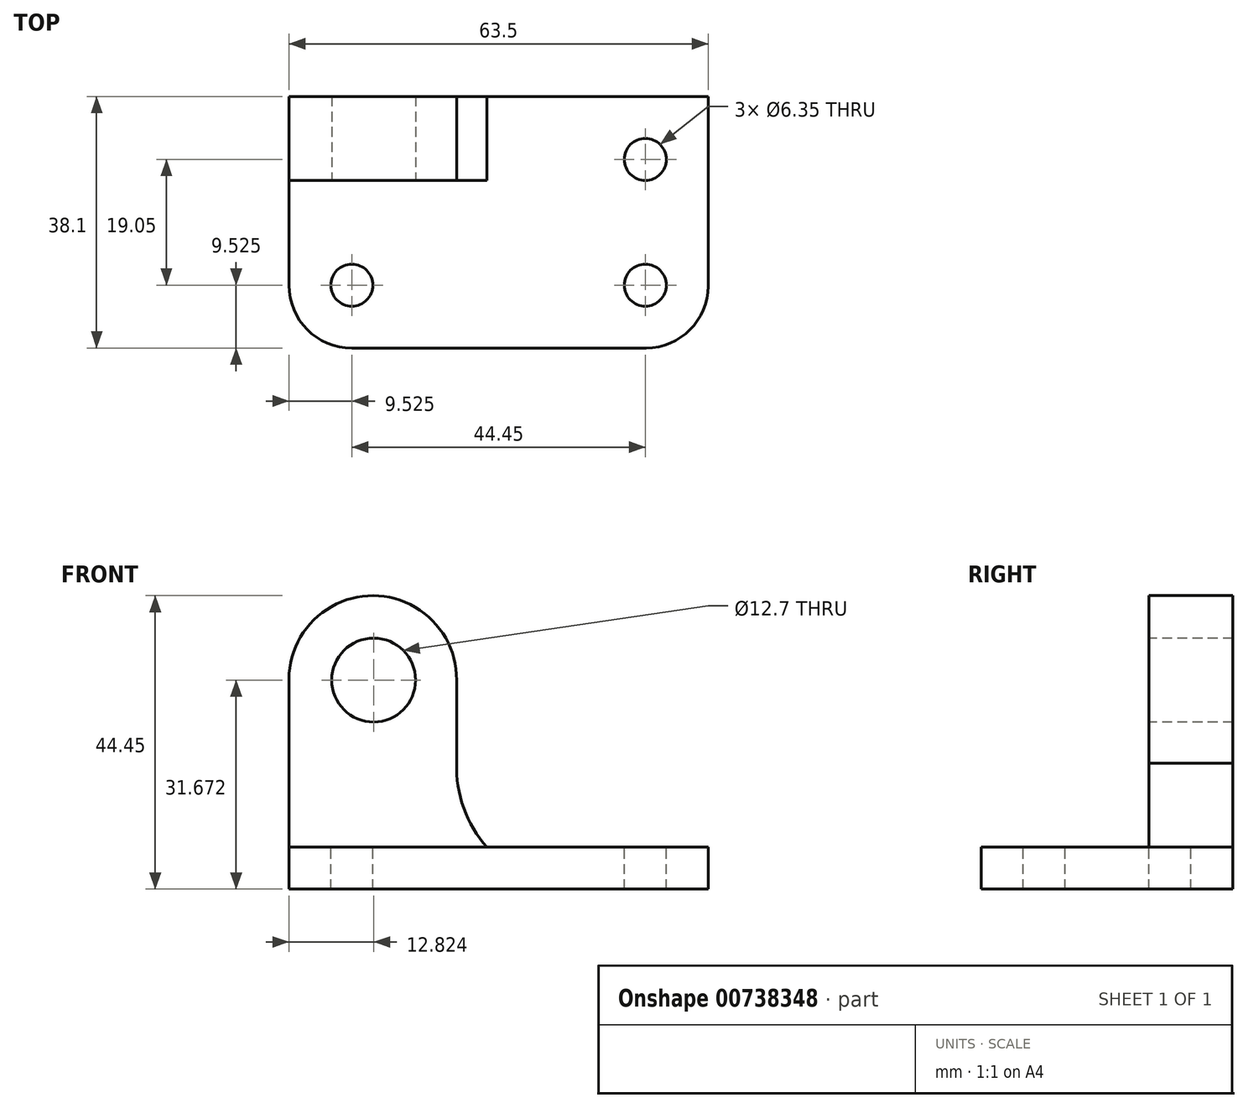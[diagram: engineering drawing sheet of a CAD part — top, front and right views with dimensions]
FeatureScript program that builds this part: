
annotation { "Feature Type Name" : "Feature", "Feature Type Description" : "" }
export const myFeature = defineFeature(function(context is Context, id is Id, definition is map)
    precondition{}
    {
        {
            var Q0;
            Q0=qCreatedBy(makeId("Right.planeOp"),FACE);
            var sketch = newSketch(context, id + "F0", { "sketchPlane" : qUnion([Q0])});
            skLineSegment(sketch, "E0", {"start": v(0, 0) * mm, "end": v(0, 44.45) * mm});
            skLineSegment(sketch, "E1", {"start": v(0, 44.45) * mm, "end": v(-12.7, 44.45) * mm});
            skLineSegment(sketch, "E2", {"start": v(-12.7, 44.45) * mm, "end": v(-12.7, 6.35) * mm});
            skLineSegment(sketch, "E3", {"start": v(-12.7, 6.35) * mm, "end": v(-38.1, 6.35) * mm});
            skLineSegment(sketch, "E4", {"start": v(-38.1, 6.35) * mm, "end": v(-38.1, 0) * mm});
            skLineSegment(sketch, "E5", {"start": v(-38.1, 0) * mm, "end": v(0, 0) * mm});
            skSolve(sketch);
        }
        {
            var Q0;
            Q0 = qSketchRegion(id + "F0", true);
            extrude(context, id + "F1", {"entities" : qUnion([Q0]), "depth" : 63.5 * mm, "offsetDistance" : 25.4 * mm});
        }
        {
            var Q0;
            Q0=makeQuery(id+"F1.opExtrude","SWEPT_FACE",FACE,{"disambiguationData":[OSD([sQuery(id+"F0.wireOp",EDGE,"E2")])]});
            var sketch = newSketch(context, id + "F2", { "sketchPlane" : qUnion([Q0])});
            skCircle(sketch, "E6", {"center": v(12.82, 31.67) * mm, "radius": 6.35 * mm});
            skArc(sketch, "E7", {"start": v(25.4, 19.1) * mm, "mid": v(26.49, 12.25) * mm, "end": v(30.03, 6.3) * mm});
            skLineSegment(sketch, "E8", {"start": v(25.4, 31.67) * mm, "end": v(25.4, 19.1) * mm});
            skLineSegment(sketch, "E9", {"start": v(0, 31.67) * mm, "end": v(0, 6.34) * mm});
            skLineSegment(sketch, "E10", {"start": v(0, 6.34) * mm, "end": v(30.03, 6.3) * mm});
            skLineSegment(sketch, "E11", {"start": v(0, 31.67) * mm, "end": v(25.4, 31.67) * mm});
            skLineSegment(sketch, "E12", {"start": v(0, 31.67) * mm, "end": v(0, 44.45) * mm});
            skArc(sketch, "E13", {"start": v(25.4, 31.67) * mm, "mid": v(12.7, 44.45) * mm, "end": v(0, 31.67) * mm});
            skSolve(sketch);
        }
        {
            var Q0;
            {var subQ0=sQuery(id+"F2.wireOp",EDGE,"E11");var subQ1=sQuery(id+"F2.wireOp",EDGE,"E6");var subQ2=makeQuery(id+"F2.imprint","INTERSECT",VERTEX,{"disambiguationData":[OD(0.0)],"derivedFrom":[subQ1,subQ0]});Q0=makeQuery(id+"F2.imprint","IMPRINT",FACE,{"disambiguationData":[TD([[makeQuery(id+"F2.imprint","IMPRINT",EDGE,{"disambiguationData":[TD([[subQ2,1.0]])],"derivedFrom":subQ1}),1.0]])]});}
            var Q1;
            {var subQ0=sQuery(id+"F2.wireOp",EDGE,"E11");var subQ1=sQuery(id+"F2.wireOp",EDGE,"E6");var subQ2=makeQuery(id+"F2.imprint","INTERSECT",VERTEX,{"disambiguationData":[OD(0.0)],"derivedFrom":[subQ1,subQ0]});Q1=makeQuery(id+"F2.imprint","IMPRINT",FACE,{"disambiguationData":[TD([[makeQuery(id+"F2.imprint","IMPRINT",EDGE,{"disambiguationData":[TD([[subQ2,-1.0]])],"derivedFrom":subQ1}),1.0]])]});}
            var Q2;
            {var subQ5=sQuery(id+"F2.wireOp",EDGE,"E8");Q2=makeQuery(id+"F2.imprint","IMPRINT",FACE,{"disambiguationData":[TD([[makeQuery(id+"F2.imprint","IMPRINT",EDGE,{"derivedFrom":subQ5}),1.0]])]});}
            extrude(context, id + "F3", {"entities" : qUnion([Q0, Q1, Q2]), "operationType" : NewBodyOperationType.REMOVE, "endBound" : BoundingType.THROUGH_ALL, "oppositeDirection" : true, "depth" : 25.4 * mm, "offsetDistance" : 25.4 * mm});
        }
        {
            var Q0;
            {var subQ0=sQuery(id+"F0.wireOp",EDGE,"E3");Q0=makeQuery(id+"F3.boolean.opBoolean","MERGE",FACE,{"derivedFrom":[makeQuery(id+"F1.opExtrude","SWEPT_FACE",FACE,{"disambiguationData":[OSD([subQ0])]}),makeQuery(id+"F3.opExtrude","SWEPT_FACE",FACE,{"disambiguationData":[OSD([sQuery(id+"F0.wireOp",EDGE,"E2"),subQ0])]})]});}
            var sketch = newSketch(context, id + "F4", { "sketchPlane" : qUnion([Q0])});
            skLineSegment(sketch, "E14", {"start": v(0, -38.1) * mm, "end": v(0, -28.58) * mm});
            skLineSegment(sketch, "E15", {"start": v(0, -28.58) * mm, "end": v(9.53, -28.58) * mm});
            skCircle(sketch, "E16", {"center": v(9.53, -28.58) * mm, "radius": 3.18 * mm});
            skArc(sketch, "E17", {"start": v(0, -28.58) * mm, "mid": v(2.79, -35.31) * mm, "end": v(9.52, -38.1) * mm});
            skLineSegment(sketch, "E18", {"start": v(63.5, -28.58) * mm, "end": v(53.98, -28.58) * mm});
            skLineSegment(sketch, "E19", {"start": v(53.98, -28.57) * mm, "end": v(53.98, -38.1) * mm});
            skCircle(sketch, "E20", {"center": v(53.98, -28.58) * mm, "radius": 3.18 * mm});
            skArc(sketch, "E21", {"start": v(53.98, -38.1) * mm, "mid": v(60.73, -35.33) * mm, "end": v(63.5, -28.58) * mm});
            skSolve(sketch);
        }
        {
            var Q0;
            Q0=makeQuery(id+"F4.imprint","IMPRINT",FACE,{"disambiguationData":[TD([[makeQuery(id+"F4.imprint","IMPRINT",EDGE,{"derivedFrom":sQuery(id+"F4.wireOp",EDGE,"E16")}),1.0]])]});
            var Q1;
            {var subQ0=sQuery(id+"F4.wireOp",EDGE,"E19");var subQ1=sQuery(id+"F4.wireOp",EDGE,"E18");var subQ2=makeQuery(id+"F4.imprint","INTERSECT",VERTEX,{"derivedFrom":[subQ1,subQ0]});Q1=makeQuery(id+"F4.imprint","IMPRINT",FACE,{"disambiguationData":[TD([[makeQuery(id+"F4.imprint","IMPRINT",EDGE,{"disambiguationData":[TD([[subQ2,1.0]])],"derivedFrom":subQ1}),-1.0]])]});}
            var Q2;
            {var subQ0=sQuery(id+"F4.wireOp",EDGE,"E19");var subQ1=sQuery(id+"F4.wireOp",EDGE,"E18");var subQ2=makeQuery(id+"F4.imprint","INTERSECT",VERTEX,{"derivedFrom":[subQ1,subQ0]});Q2=makeQuery(id+"F4.imprint","IMPRINT",FACE,{"disambiguationData":[TD([[makeQuery(id+"F4.imprint","IMPRINT",EDGE,{"disambiguationData":[TD([[subQ2,1.0]])],"derivedFrom":subQ1}),1.0]])]});}
            var Q3;
            {var subQ0=sQuery(id+"F4.wireOp",EDGE,"E21");var subQ1=makeQuery(id+"F1.opExtrude","SWEPT_EDGE",EDGE,{"disambiguationData":[OSD([sQuery(id+"F0.wireOp",EDGE,"E3"),sQuery(id+"F0.wireOp",EDGE,"E4")])]});var subQ3=makeQuery(id+"F4.imprint","INTERSECT",VERTEX,{"derivedFrom":[subQ1,subQ0]});Q3=makeQuery(id+"F4.imprint","IMPRINT",FACE,{"disambiguationData":[TD([[makeQuery(id+"F4.imprint","IMPRINT",EDGE,{"disambiguationData":[TD([[subQ3,1.0]])],"derivedFrom":subQ0}),1.0]])]});}
            var Q4;
            {var subQ0=sQuery(id+"F4.wireOp",EDGE,"E21");var subQ1=sQuery(id+"F0.wireOp",EDGE,"E3");var subQ2=makeQuery(id+"F3.boolean.opBoolean","MERGE",EDGE,{"derivedFrom":[makeQuery(id+"F1.opExtrude","CAP_EDGE",EDGE,{"disambiguationData":[OSD([subQ1])],"isStart":false}),makeQuery(id+"F3.opExtrude","SWEPT_EDGE",EDGE,{"disambiguationData":[OSD([sQuery(id+"F0.wireOp",EDGE,"E2"),subQ1])]})]});var subQ4=makeQuery(id+"F4.imprint","INTERSECT",VERTEX,{"derivedFrom":[subQ2,subQ0]});Q4=makeQuery(id+"F4.imprint","IMPRINT",FACE,{"disambiguationData":[TD([[makeQuery(id+"F4.imprint","IMPRINT",EDGE,{"disambiguationData":[TD([[subQ4,-1.0]])],"derivedFrom":subQ0}),1.0]])]});}
            var Q5;
            {var subQ0=sQuery(id+"F4.wireOp",EDGE,"E14");Q5=makeQuery(id+"F4.imprint","IMPRINT",FACE,{"disambiguationData":[TD([[makeQuery(id+"F4.imprint","IMPRINT",EDGE,{"derivedFrom":subQ0}),1.0]])]});}
            var Q6;
            {var subQ0=sQuery(id+"F4.wireOp",EDGE,"E21");var subQ1=sQuery(id+"F0.wireOp",EDGE,"E3");var subQ2=makeQuery(id+"F1.opExtrude","SWEPT_EDGE",EDGE,{"disambiguationData":[OSD([subQ1,sQuery(id+"F0.wireOp",EDGE,"E4")])]});var subQ3=makeQuery(id+"F4.imprint","INTERSECT",VERTEX,{"derivedFrom":[subQ2,subQ0]});Q6=makeQuery(id+"F4.imprint","IMPRINT",FACE,{"disambiguationData":[TD([[makeQuery(id+"F4.imprint","IMPRINT",EDGE,{"disambiguationData":[TD([[subQ3,-1.0]])],"derivedFrom":subQ0}),-1.0]])]});}
            extrude(context, id + "F5", {"entities" : qUnion([Q0, Q1, Q2, Q3, Q4, Q5, Q6]), "operationType" : NewBodyOperationType.REMOVE, "endBound" : BoundingType.THROUGH_ALL, "oppositeDirection" : true, "depth" : 25.4 * mm, "offsetDistance" : 25.4 * mm});
        }
        {
            var Q0;
            {var subQ0=sQuery(id+"F0.wireOp",EDGE,"E3");Q0=makeQuery(id+"F3.boolean.opBoolean","MERGE",FACE,{"derivedFrom":[makeQuery(id+"F1.opExtrude","SWEPT_FACE",FACE,{"disambiguationData":[OSD([subQ0])]}),makeQuery(id+"F3.opExtrude","SWEPT_FACE",FACE,{"disambiguationData":[OSD([sQuery(id+"F0.wireOp",EDGE,"E2"),subQ0])]})]});}
            var sketch = newSketch(context, id + "F6", { "sketchPlane" : qUnion([Q0])});
            skLineSegment(sketch, "E22", {"start": v(53.98, -28.57) * mm, "end": v(53.98, 0) * mm});
            skLineSegment(sketch, "E23", {"start": v(53.98, 0) * mm, "end": v(53.98, -9.53) * mm});
            skCircle(sketch, "E24", {"center": v(53.98, -9.53) * mm, "radius": 3.18 * mm});
            skSolve(sketch);
        }
        {
            var Q0;
            Q0 = qSketchRegion(id + "F6", true);
            extrude(context, id + "F7", {"entities" : qUnion([Q0]), "operationType" : NewBodyOperationType.REMOVE, "endBound" : BoundingType.THROUGH_ALL, "oppositeDirection" : true, "depth" : 25.4 * mm, "offsetDistance" : 25.4 * mm});
        }
    });
